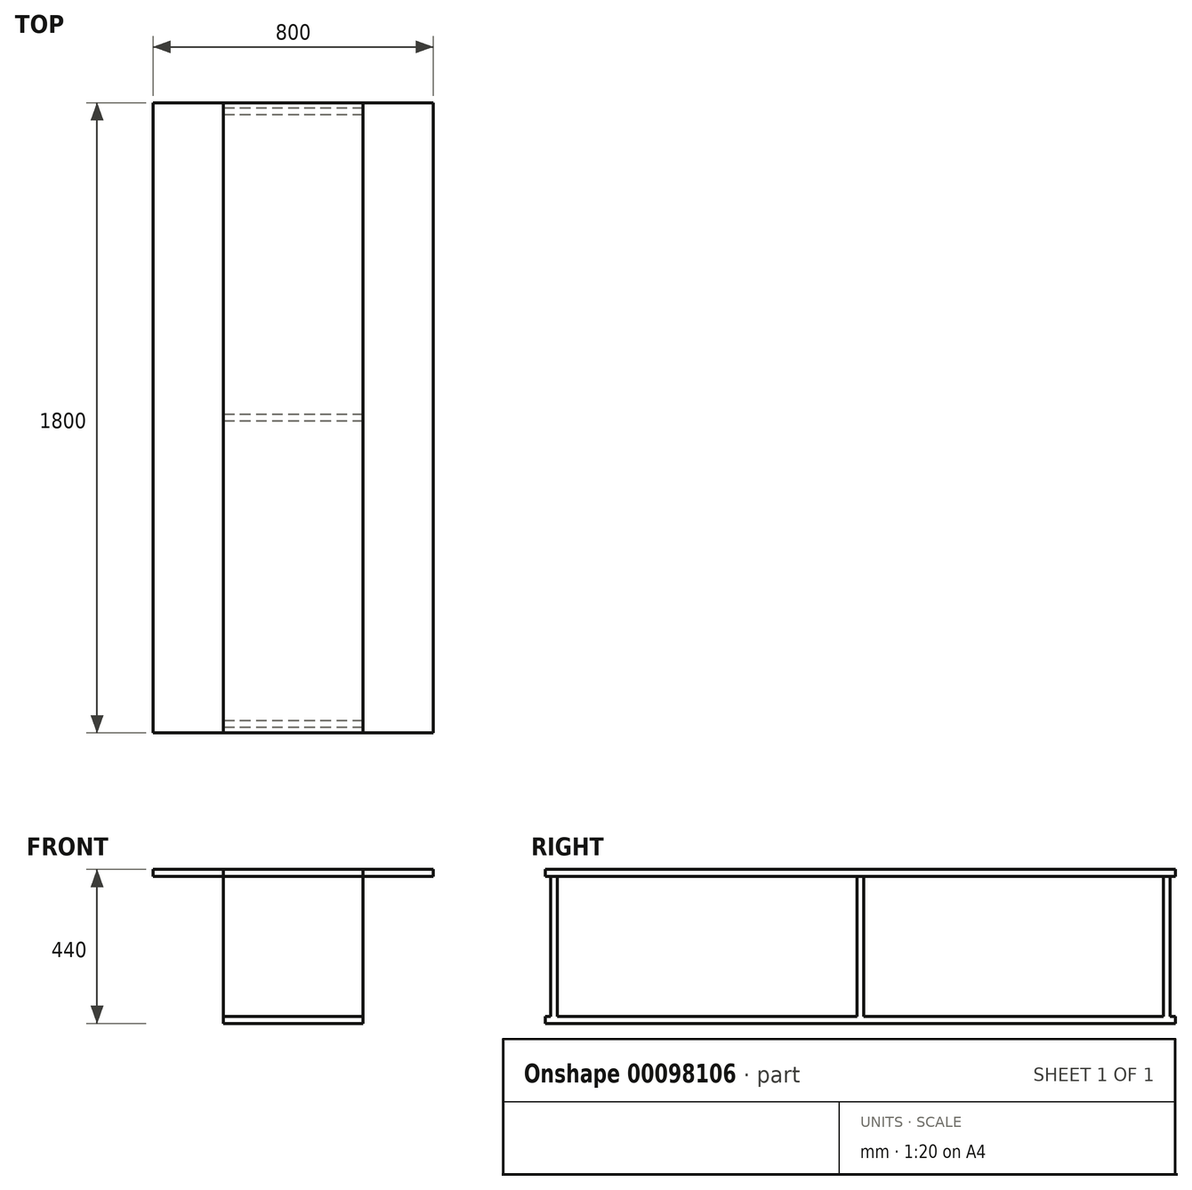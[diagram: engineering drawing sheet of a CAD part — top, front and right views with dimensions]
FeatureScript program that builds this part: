
annotation { "Feature Type Name" : "Feature", "Feature Type Description" : "" }
export const myFeature = defineFeature(function(context is Context, id is Id, definition is map)
    precondition{}
    {
        {
            var Q0;
            Q0=qCreatedBy(makeId("Top.planeOp"),FACE);
            var sketch = newSketch(context, id + "F0", { "sketchPlane" : qUnion([Q0])});
            skLineSegment(sketch, "E0.bottom", {"start": v(200, -900) * mm, "end": v(-200, -900) * mm});
            skLineSegment(sketch, "E0.top", {"start": v(200, 900) * mm, "end": v(-200, 900) * mm});
            skLineSegment(sketch, "E0.left", {"start": v(200, -900) * mm, "end": v(200, 900) * mm});
            skLineSegment(sketch, "E0.right", {"start": v(-200, -900) * mm, "end": v(-200, 900) * mm});
            skPoint(sketch, "E0.middle", {"position": v(0, 0) * mm});
            skSolve(sketch);
        }
        {
            var Q0;
            Q0 = qSketchRegion(id + "F0", true);
            extrude(context, id + "F1", {"entities" : qUnion([Q0]), "depth" : 20 * mm});
        }
        {
            var Q0;
            Q0=makeQuery(id+"F1.opExtrude","CAP_FACE",FACE,{"disambiguationData":[OSD([sQuery(id+"F0.wireOp",EDGE,"E0.bottom"),sQuery(id+"F0.wireOp",EDGE,"E0.top"),sQuery(id+"F0.wireOp",EDGE,"E0.left"),sQuery(id+"F0.wireOp",EDGE,"E0.right")])],"isStart":true});
            var sketch = newSketch(context, id + "F2", { "sketchPlane" : qUnion([Q0])});
            skLineSegment(sketch, "E1.bottom", {"start": v(200, -10) * mm, "end": v(-200, -10) * mm});
            skLineSegment(sketch, "E1.top", {"start": v(200, 10) * mm, "end": v(-200, 10) * mm});
            skLineSegment(sketch, "E1.left", {"start": v(200, -10) * mm, "end": v(200, 10) * mm});
            skLineSegment(sketch, "E1.right", {"start": v(-200, -10) * mm, "end": v(-200, 10) * mm});
            skPoint(sketch, "E1.middle", {"position": v(0, 0) * mm});
            skLineSegment(sketch, "E2.bottom", {"start": v(200, 865) * mm, "end": v(-200, 865) * mm});
            skLineSegment(sketch, "E2.top", {"start": v(200, 885) * mm, "end": v(-200, 885) * mm});
            skLineSegment(sketch, "E2.left", {"start": v(200, 865) * mm, "end": v(200, 885) * mm});
            skLineSegment(sketch, "E2.right", {"start": v(-200, 865) * mm, "end": v(-200, 885) * mm});
            skPoint(sketch, "E2.middle", {"position": v(0, 875) * mm});
            skLineSegment(sketch, "E3.bottom", {"start": v(200, -885) * mm, "end": v(-200, -885) * mm});
            skLineSegment(sketch, "E3.top", {"start": v(200, -865) * mm, "end": v(-200, -865) * mm});
            skLineSegment(sketch, "E3.left", {"start": v(200, -885) * mm, "end": v(200, -865) * mm});
            skLineSegment(sketch, "E3.right", {"start": v(-200, -885) * mm, "end": v(-200, -865) * mm});
            skPoint(sketch, "E3.middle", {"position": v(0, -875) * mm});
            skLineSegment(sketch, "E4", {"start": v(200, 0) * mm, "end": v(-200, 0) * mm, "construction": true});
            skSolve(sketch);
        }
        {
            var Q0;
            Q0 = qSketchRegion(id + "F2", true);
            extrude(context, id + "F3", {"entities" : qUnion([Q0]), "operationType" : NewBodyOperationType.ADD, "depth" : 400 * mm});
        }
        {
            var Q0;
            Q0=makeQuery(id+"F3.opExtrude","CAP_FACE",FACE,{"disambiguationData":[OSD([sQuery(id+"F2.wireOp",EDGE,"E1.bottom"),sQuery(id+"F2.wireOp",EDGE,"E1.top"),sQuery(id+"F2.wireOp",EDGE,"E1.left"),sQuery(id+"F2.wireOp",EDGE,"E1.right")])],"isStart":false});
            var sketch = newSketch(context, id + "F4", { "sketchPlane" : qUnion([Q0])});
            skLineSegment(sketch, "E5.bottom", {"start": v(200, -900) * mm, "end": v(-200, -900) * mm});
            skLineSegment(sketch, "E5.top", {"start": v(200, 900) * mm, "end": v(-200, 900) * mm});
            skLineSegment(sketch, "E5.left", {"start": v(200, -900) * mm, "end": v(200, 900) * mm});
            skLineSegment(sketch, "E5.right", {"start": v(-200, -900) * mm, "end": v(-200, 900) * mm});
            skPoint(sketch, "E5.middle", {"position": v(0, 0) * mm});
            skSolve(sketch);
        }
        {
            var Q0;
            Q0 = qSketchRegion(id + "F4", true);
            extrude(context, id + "F5", {"entities" : qUnion([Q0]), "operationType" : NewBodyOperationType.ADD, "depth" : 20 * mm});
        }
        {
            var Q0;
            Q0=qCreatedBy(makeId("Top.planeOp"),FACE);
            var sketch = newSketch(context, id + "F6", { "sketchPlane" : qUnion([Q0])});
            skLineSegment(sketch, "E6.bottom", {"start": v(-200, 900) * mm, "end": v(-400, 900) * mm});
            skLineSegment(sketch, "E6.top", {"start": v(-200, -900) * mm, "end": v(-400, -900) * mm});
            skLineSegment(sketch, "E6.left", {"start": v(-200, 900) * mm, "end": v(-200, -900) * mm});
            skLineSegment(sketch, "E6.right", {"start": v(-400, 900) * mm, "end": v(-400, -900) * mm});
            skLineSegment(sketch, "E7.bottom", {"start": v(200, -900) * mm, "end": v(400, -900) * mm});
            skLineSegment(sketch, "E7.top", {"start": v(200, 900) * mm, "end": v(400, 900) * mm});
            skLineSegment(sketch, "E7.left", {"start": v(200, -900) * mm, "end": v(200, 900) * mm});
            skLineSegment(sketch, "E7.right", {"start": v(400, -900) * mm, "end": v(400, 900) * mm});
            skSolve(sketch);
        }
        {
            var Q0;
            Q0 = qSketchRegion(id + "F6", true);
            extrude(context, id + "F7", {"entities" : qUnion([Q0]), "depth" : 20 * mm});
        }
    });
